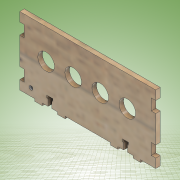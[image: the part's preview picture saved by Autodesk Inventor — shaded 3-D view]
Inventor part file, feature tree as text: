
AUTODESK INVENTOR PART (.ipt)
format: ipt  version: 2022 (Build 260153000, 153)  size: 250,880 bytes
history: native  units: mm
features: extrude x4, sketch x4, other x1
ambient origin geometry x8: Origin, YZ Plane, XZ Plane, XY Plane, X Axis, Y Axis, Z Axis, Center Point
bodies: Body1 (feature_tree)
feature tree (9):
  other  "Sólido1"
  extrude  "Extrusión1"  Depth=90.0mm
  sketch  "Boceto4"  dims[d4=50.0mm d6=35.8mm]
  sketch  "Boceto5"  dims[d7=35.8mm d8=35.8mm]
  extrude  "Extrusión2"  Depth=50.0mm
  extrude  "Extrusión3"  Depth=35.8mm
  extrude  "Extrusión5"  Depth=6.0mm TaperAngle=0.0deg
  sketch  "Boceto3"  dims[d1=90.0mm d3=22.0mm]
  sketch  "Boceto7"  dims[d9=35.0mm d10=6.0mm d11=0.0mm d12=8.0mm d13=3.1mm d14=5.0mm d15=12.0mm d16=40.0mm d17=10.0mm d18=10.0mm d19=20.0mm d20=20.0mm d21=0.0mm d22=0.0mm d23=3.0mm d24=0.0mm d31=6.0mm d32=15.0mm d33=12.0mm d34=0.0mm d35=0.0mm d37=5.0mm d38=10.0mm d39=15.0mm d40=180.0mm]
